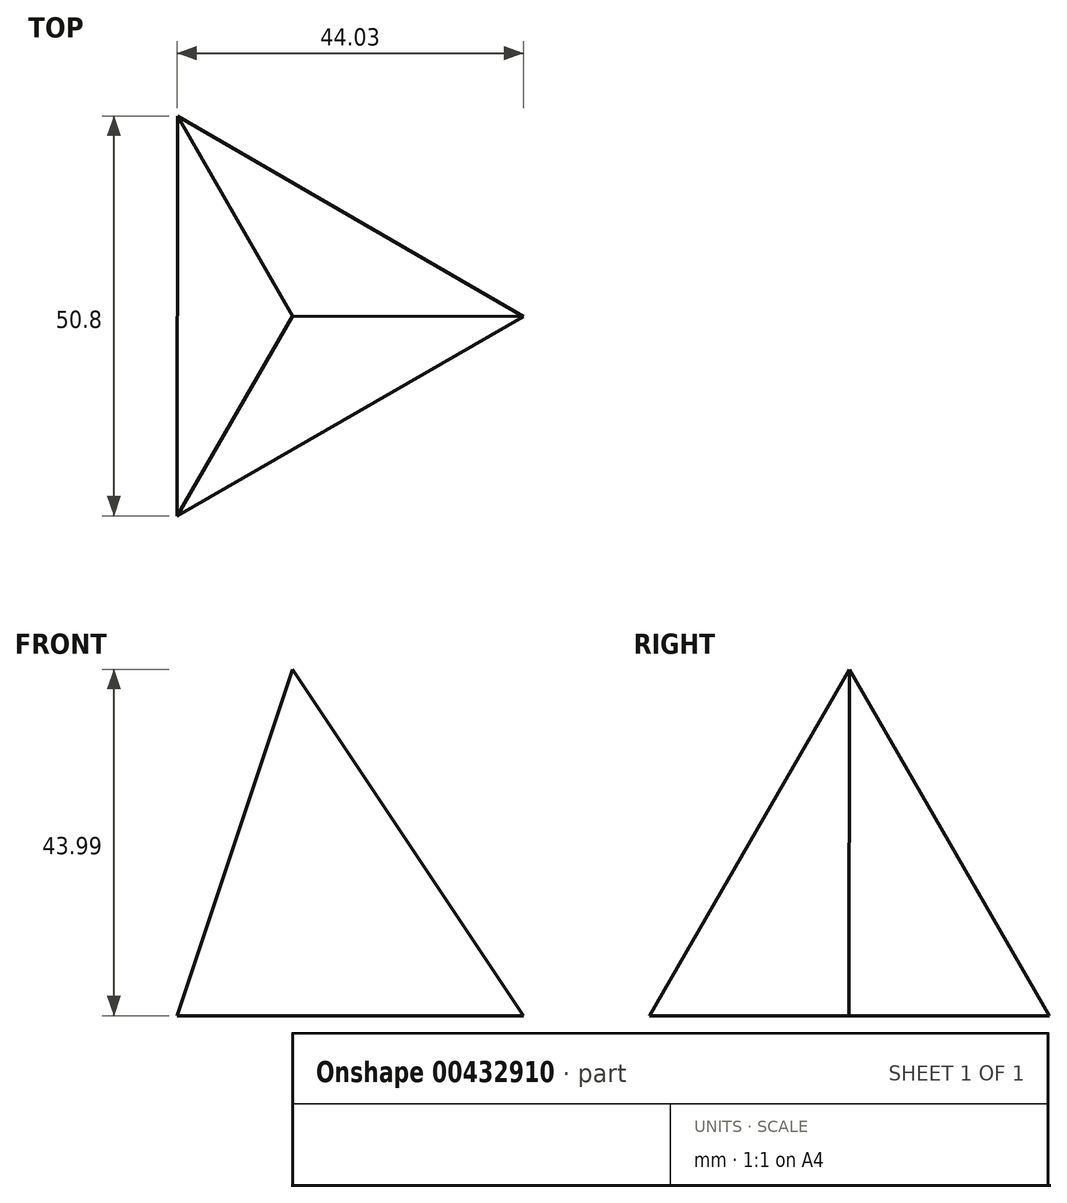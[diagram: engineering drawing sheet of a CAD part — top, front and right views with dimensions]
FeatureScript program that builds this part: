
annotation { "Feature Type Name" : "Feature", "Feature Type Description" : "" }
export const myFeature = defineFeature(function(context is Context, id is Id, definition is map)
    precondition{}
    {
        {
            var Q0;
            Q0=qCreatedBy(makeId("Top.planeOp"),FACE);
            var sketch = newSketch(context, id + "F0", { "sketchPlane" : qUnion([Q0])});
            skCircle(sketch, "E0.cCircle", {"center": v(0, 0) * mm, "radius": 14.66 * mm, "construction": true});
            skLineSegment(sketch, "E0.0", {"start": v(29.33, -0.04) * mm, "end": v(-14.7, -25.38) * mm});
            skLineSegment(sketch, "E0.1", {"start": v(-14.7, -25.38) * mm, "end": v(-14.63, 25.42) * mm});
            skLineSegment(sketch, "E0.2", {"start": v(-14.63, 25.42) * mm, "end": v(29.33, -0.04) * mm});
            skPoint(sketch, "E0.0.midPoint", {"position": v(7.32, -12.7) * mm});
            skLineSegment(sketch, "E1", {"start": v(-14.63, 25.42) * mm, "end": v(7.32, -12.7) * mm, "construction": true});
            skLineSegment(sketch, "E2", {"start": v(29.33, -0.04) * mm, "end": v(-14.66, -0.04) * mm, "construction": true});
            skLineSegment(sketch, "E3", {"start": v(-14.7, -25.38) * mm, "end": v(7.35, 12.7) * mm, "construction": true});
            skSolve(sketch);
        }
        {
            var Q0;
            Q0=qCreatedBy(makeId("Top.planeOp"),FACE);
            cPlane(context, id + "F1", {"entities" : qUnion([Q0]), "cplaneType" : CPlaneType.OFFSET, "offset" : 44 * mm, "width" : 152.4 * mm, "height" : 152.4 * mm});
        }
        {
            var Q0;
            Q0=qCreatedBy(id+"F1.planeOp",FACE);
            var sketch = newSketch(context, id + "F2", { "sketchPlane" : qUnion([Q0])});
            skPoint(sketch, "E4", {"position": v(0, 0) * mm});
            skSolve(sketch);
        }
        {
            var Q0;
            Q0=sQuery(id+"F2.wireOp",VERTEX,"E4");
            var Q1;
            Q1 = qSketchRegion(id + "F0", true);
            loft(context, id + "F3", {"sheetProfilesArray" : [{ "sheetProfileEntities" : qUnion([Q0]) }, { "sheetProfileEntities" : qUnion([Q1]) }]});
        }
    });
